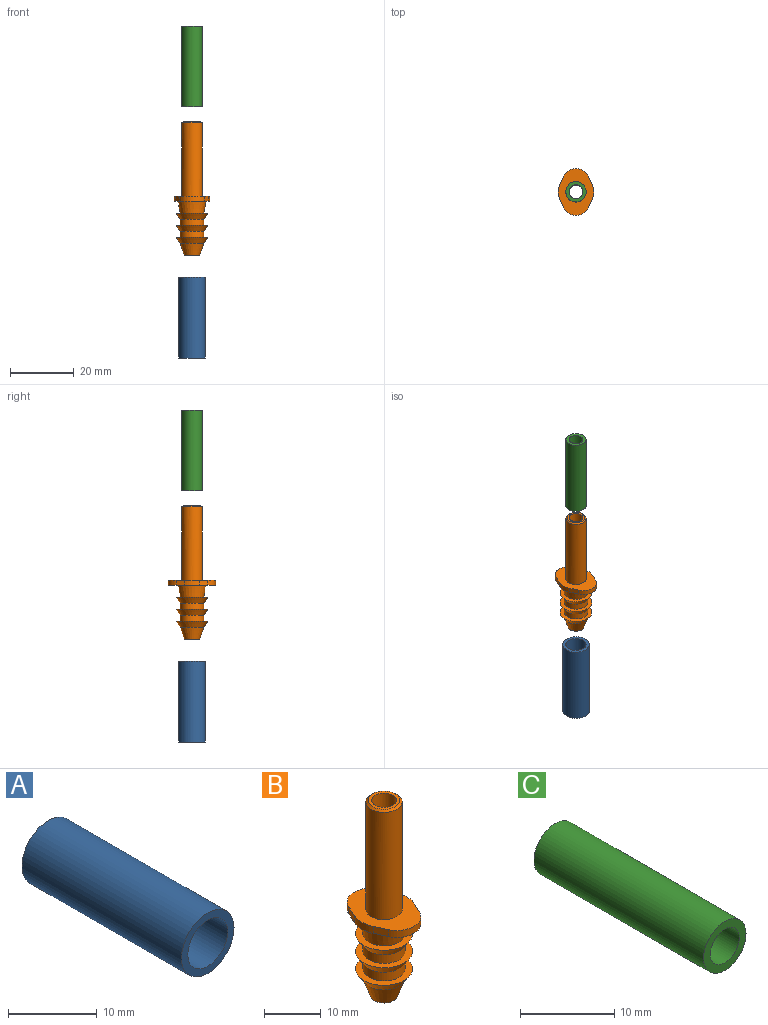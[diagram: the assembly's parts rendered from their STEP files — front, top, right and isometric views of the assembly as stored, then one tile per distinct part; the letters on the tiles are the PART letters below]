
ASSEMBLY  parts=3 mates=2
PART A: 4 faces, bbox 8.4x25.4x8.4 mm
  f0: cylinder r=3.17mm len=25.4mm, axis (0,1,0), area 506.7mm2, adj f2,f3
  f1: cylinder r=4.17mm len=25.4mm, axis (0,1,0), area 666.3mm2, adj f2,f3
  f2: plane 8.35x8.35mm, normal (0,-1,0), area 23.1mm2, adj f0,f1
  f3: plane 8.35x8.35mm, normal (0,1,0), area 23.1mm2, adj f0,f1
PART B: 25 faces, bbox 11.1x14.8x42 mm
  f0: plane 14.8x11.1mm, normal (0,0,1), area 92mm2, adj f3,f17,f18,f19,f20,f21,f22,f23
  f1: plane 14.8x11.1mm, normal (0,0,-1), area 63.9mm2, adj f4,f17,f18,f19,f20,f21,f22,f23
  f2: plane 5.59x5.59mm, normal (0,0,1), area 9.7mm2, adj f15,f16
  f3: cylinder r=3.17mm len=23.12mm, axis (0,0,1), area 461.2mm2, adj f0,f16
  f4: cone r=3.7mm half-angle=9.9deg, axis (0,0,1), area 97.1mm2, adj f1,f5
  f5: plane 10.04x10.04mm, normal (0,0,1), area 36.1mm2, adj f4,f6
  f6: cone r=3.7mm half-angle=34.9deg, axis (0,0,1), area 63.1mm2, adj f5,f7
  f7: cylinder r=3.7mm len=7.4mm, axis (0,0,1), area 43.9mm2, adj f6,f8
  f8: plane 10.04x10.04mm, normal (0,0,1), area 36.1mm2, adj f7,f9
  f9: cone r=3.7mm half-angle=34.9deg, axis (0,0,1), area 63.1mm2, adj f8,f10
  f10: cylinder r=3.7mm len=7.4mm, axis (0,0,1), area 43.9mm2, adj f9,f11
  f11: plane 10.04x10.04mm, normal (0,0,1), area 36.1mm2, adj f10,f12
  f12: cone r=3.7mm half-angle=34.9deg, axis (0,0,1), area 63.1mm2, adj f11,f13
  f13: cone r=2.38mm half-angle=19.2deg, axis (0,0,1), area 76.4mm2, adj f12,f14
  f14: plane 4.76x4.76mm, normal (0,0,-1), area 3mm2, adj f13,f15
  f15: cylinder r=2.17mm len=42mm, axis (0,0,1), area 574mm2, adj f2,f14
  f16: cone r=2.79mm half-angle=45deg, axis (0,0,-1), area 10.1mm2, adj f2,f3
  f17: cylinder r=4.22mm len=7.68mm, axis (0,0,1), area 14.5mm2, adj f0,f1,f18,f24
  f18: plane 2.62x1.5mm, normal (-0.91,-0.42,0), area 4.3mm2, adj f0,f1,f17,f19
  f19: cylinder r=5.55mm len=4.63mm, axis (0,0,1), area 7.2mm2, adj f0,f1,f18,f20
  f20: plane 2.62x1.5mm, normal (-0.91,0.42,0), area 4.3mm2, adj f0,f1,f19,f21
  f21: cylinder r=4.22mm len=7.68mm, axis (0,0,1), area 14.5mm2, adj f0,f1,f20,f22
  f22: plane 2.62x1.5mm, normal (0.91,0.42,0), area 4.3mm2, adj f0,f1,f21,f23
  f23: cylinder r=5.55mm len=4.63mm, axis (0,0,1), area 7.2mm2, adj f0,f1,f22,f24
  f24: plane 2.62x1.5mm, normal (0.91,-0.42,0), area 4.3mm2, adj f0,f1,f17,f23
PART C: 4 faces, bbox 6.4x25.4x6.4 mm
  f0: cylinder r=2.17mm len=25.4mm, axis (0,1,0), area 347.1mm2, adj f2,f3
  f1: cylinder r=3.17mm len=25.4mm, axis (0,1,0), area 506.7mm2, adj f2,f3
  f2: plane 6.35x6.35mm, normal (0,-1,0), area 16.8mm2, adj f0,f1
  f3: plane 6.35x6.35mm, normal (0,1,0), area 16.8mm2, adj f0,f1
PLACE A rot(axis=(-1,0,0),90deg) t=(2.82,-19.32,-74.33)mm
PLACE B t=(2.82,-19.32,-21.14)mm fixed
PLACE C rot(axis=(1,0,0),90deg) t=(2.82,-19.32,29.85)mm
MATE slider A.f0 <-> B.f3  axis (0,0,1) through (2.82,-19.32,-48.93)mm
MATE slider C.f0 <-> B.f3  axis (0,0,1) through (2.82,-19.32,29.85)mm
